# Revit family: EKF_EE_КожухРубильникаВРУ_UNIT_PROxima
name_source: partatom
category: Электрооборудование
units: mm (PartAtom-declared; Revit-internal decimal feet)

## family parameters
Всегда вертикально = Нет
На основе рабочей плоскости = Да
Общий = Нет
При загрузке вырезать с полостями = Нет
Размер круглого соединителя = Использовать диаметр
Тип детали = Силовой щит
Точка расчета площади = Нет

## types (2) — shared parameters
ADSK_Единица измерения = шт.
ADSK_Завод-изготовитель = EKF
ADSK_Количество = 1
ADSK_Марка = Кожух рубильника
ADSK_Материал = RAL 7035_Сталь
ADSK_Обозначение = Кожух рубильника
ADSK_Размер_Высота = 190 мм
ADSK_Размер_Глубина = 25 мм
ADSK_Размер_Ширина = 175 мм
R = 2.5 мм
a = 25 мм
b = 175 мм
h = 190 мм
t = 1.2 мм
Изготовитель = EKF
Серия номенклатуры = Unit PROxima
Степень защиты IP = -
ТВ = EKF_2
Тип установки = -
zero-valued in all types: ADSK_Масса, Отметка по умолчанию

## per-type parameters (varying)
| type | ADSK_Код изделия | Тип | Типоразмер |
| Кожух рубильника ВР-32У на 100-250А для ВРУ Unit EKF PROxima | mb-15-krv-1 | 17 мм | EKF_EE_КожухРубильникаВРУUNIT_PROxima : ВР-32У на 100-250А |
| Кожух рубильника ВР-32У на 400-630А для ВРУ Unit EKF PROxima | mb-15-krv-2 | 18 мм | EKF_EE_КожухРубильникаВРУUNIT_PROxima : ВР-32У на 400-630А |

note: column(s) folded — value = type name in every type: ADSK_Наименование
